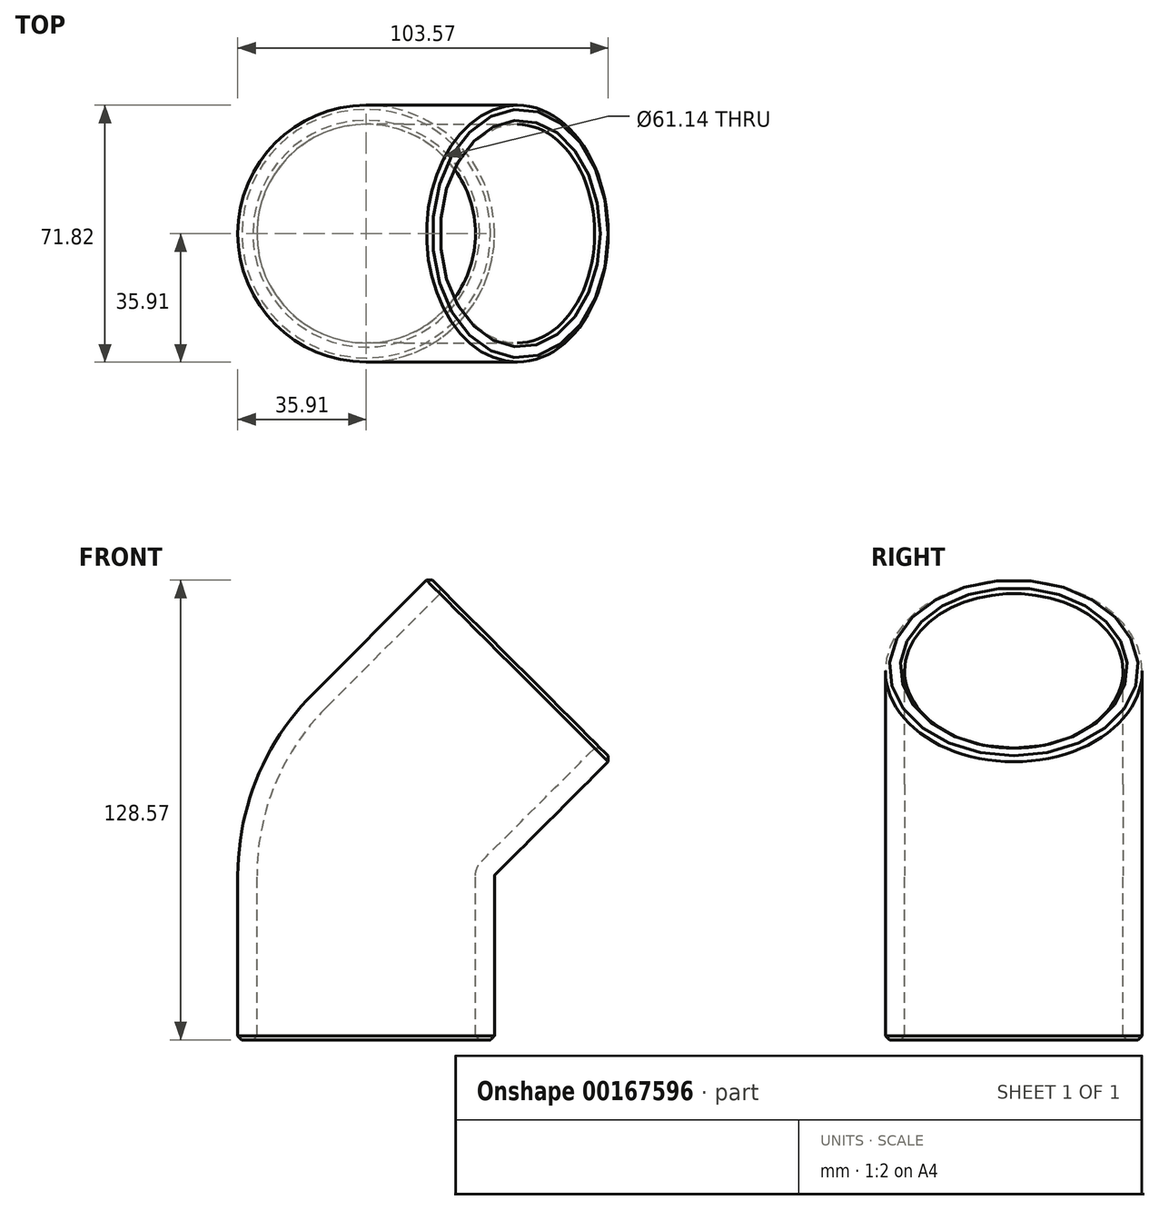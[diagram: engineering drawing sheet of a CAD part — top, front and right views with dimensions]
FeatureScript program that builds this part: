
annotation { "Feature Type Name" : "Feature", "Feature Type Description" : "" }
export const myFeature = defineFeature(function(context is Context, id is Id, definition is map)
    precondition{}
    {
        {
            var Q0;
            Q0=qCreatedBy(makeId("Front.planeOp"),FACE);
            var sketch = newSketch(context, id + "F0", { "sketchPlane" : qUnion([Q0])});
            skLineSegment(sketch, "E0", {"start": v(24.77, -42) * mm, "end": v(24.77, -10.26) * mm});
            skLineSegment(sketch, "E1", {"start": v(24.77, -10.26) * mm, "end": v(47.22, 12.2) * mm});
            skLineSegment(sketch, "E2.0", {"start": v(7.3, 7.3) * mm, "end": v(29.7, 29.7) * mm});
            skLineSegment(sketch, "E2.1", {"start": v(0, -42) * mm, "end": v(0, -10.31) * mm});
            skLineSegment(sketch, "E3", {"start": v(47.22, 12.2) * mm, "end": v(22.21, 37.2) * mm, "construction": true});
            skLineSegment(sketch, "E4", {"start": v(24.77, -42) * mm, "end": v(-17.96, -42) * mm, "construction": true});
            skPoint(sketch, "E5.visualSharp", {"position": v(0, 0) * mm});
            skArc(sketch, "E5.filletArc", {"start": v(7.3, 7.3) * mm, "mid": v(1.9, -0.78) * mm, "end": v(0, -10.31) * mm});
            skSolve(sketch);
        }
        {
            var Q0;
            Q0=sQuery(id+"F0.wireOp",VERTEX,"E2.1.start");
            var Q1;
            Q1=qCreatedBy(makeId("Top.planeOp"),FACE);
            cPlane(context, id + "F1", {"entities" : qUnion([Q0, Q1]), "cplaneType" : CPlaneType.PLANE_POINT, "offset" : 152.4 * mm, "width" : 152.4 * mm, "height" : 152.4 * mm});
        }
        {
            var Q0;
            Q0=qCreatedBy(id+"F1.planeOp",FACE);
            var sketch = newSketch(context, id + "F2", { "sketchPlane" : qUnion([Q0])});
            skCircle(sketch, "E6", {"center": v(0, 0) * mm, "radius": 21.08 * mm});
            skCircle(sketch, "E7", {"center": v(0, 0) * mm, "radius": 24.77 * mm});
            skSolve(sketch);
        }
        {
            var Q0;
            Q0=makeQuery(id+"F2.imprint","IMPRINT",FACE,{"disambiguationData":[TD([[makeQuery(id+"F2.imprint","IMPRINT",EDGE,{"derivedFrom":sQuery(id+"F2.wireOp",EDGE,"E6")}),-1.0]])]});
            var Q1;
            Q1=sQuery(id+"F0.wireOp",EDGE,"E2.1");
            var Q2;
            Q2=sQuery(id+"F0.wireOp",EDGE,"E5.filletArc");
            var Q3;
            Q3=sQuery(id+"F0.wireOp",EDGE,"E2.0");
            sweep(context, id + "F3", {"profiles" : qUnion([Q0]), "path" : qUnion([Q1, Q2, Q3])});
        }
        {
            var Q0;
            Q0=makeQuery(id+"F3.opSweep","CAP_EDGE",EDGE,{"disambiguationData":[OSD([sQuery(id+"F0.wireOp",VERTEX,"E2.0.end"),sQuery(id+"F2.wireOp",EDGE,"E7")])],"isStart":false});
            var Q1;
            Q1=makeQuery(id+"F3.opSweep","CAP_EDGE",EDGE,{"disambiguationData":[OSD([sQuery(id+"F0.wireOp",VERTEX,"E2.0.end"),sQuery(id+"F2.wireOp",EDGE,"E6")])],"isStart":false});
            var Q2;
            Q2=makeQuery(id+"F3.opSweep","CAP_EDGE",EDGE,{"disambiguationData":[OSD([sQuery(id+"F0.wireOp",VERTEX,"E2.1.start"),sQuery(id+"F2.wireOp",EDGE,"E6")])],"isStart":true});
            var Q3;
            Q3=makeQuery(id+"F3.opSweep","CAP_EDGE",EDGE,{"disambiguationData":[OSD([sQuery(id+"F0.wireOp",VERTEX,"E2.1.start"),sQuery(id+"F2.wireOp",EDGE,"E7")])],"isStart":true});
            chamfer(context, id + "F4", {"entities" : qUnion([Q0, Q1, Q2, Q3]), "width" : 0.79 * mm, "tangentPropagation" : true});
        }
        {
            var Q0;
            Q0=makeQuery(id+"F3.opSweep","SWEPT_BODY",BODY,{"disambiguationData":[OSD([sQuery(id+"F0.wireOp",EDGE,"E2.0"),sQuery(id+"F2.wireOp",EDGE,"E6"),sQuery(id+"F2.wireOp",EDGE,"E7")])]});
            var Q1;
            Q1=qCreatedBy(makeId("Origin.pointOp"),VERTEX);
            transform(context, id + "F5", {"entities" : qUnion([Q0]), "transformType" : TransformType.SCALE_UNIFORMLY, "scale" : 1.45, "scalePoint" : qUnion([Q1]), "makeCopy" : false});
        }
    });
